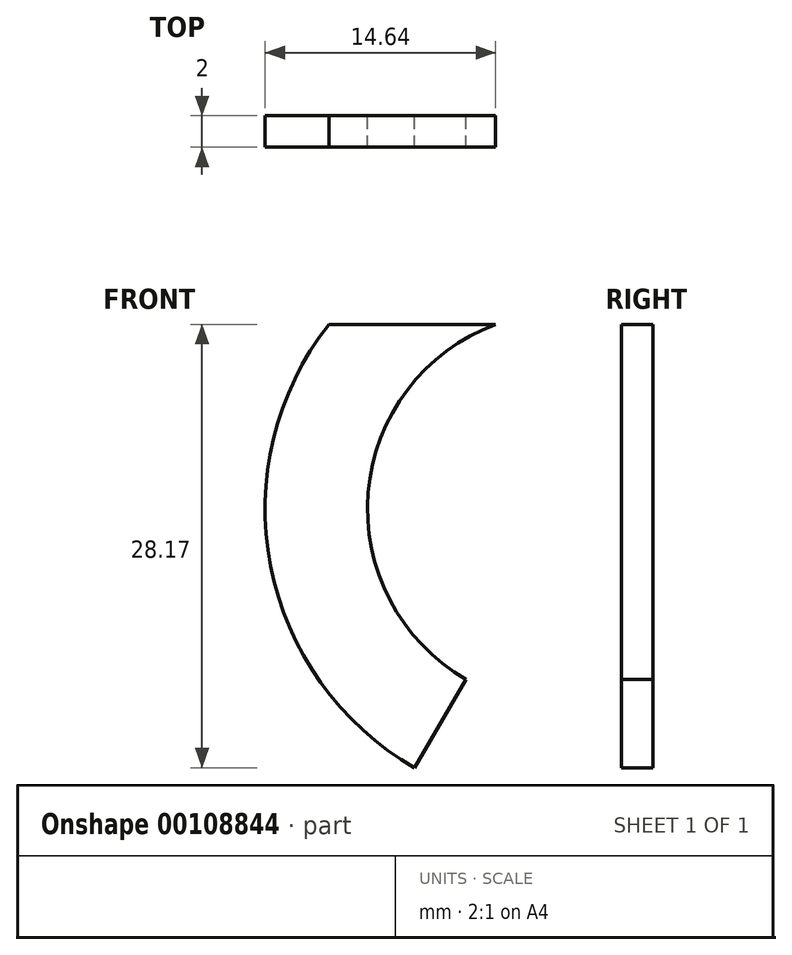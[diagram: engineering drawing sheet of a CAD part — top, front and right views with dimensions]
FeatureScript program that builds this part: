
annotation { "Feature Type Name" : "Feature", "Feature Type Description" : "" }
export const myFeature = defineFeature(function(context is Context, id is Id, definition is map)
    precondition{}
    {
        {
            var Q0;
            Q0=qCreatedBy(makeId("Front.planeOp"),FACE);
            var sketch = newSketch(context, id + "F0", { "sketchPlane" : qUnion([Q0])});
            skLineSegment(sketch, "E0", {"start": v(0, 23.45) * mm, "end": v(0, -32.3) * mm, "construction": true});
            skLineSegment(sketch, "E1", {"start": v(-31.08, 0) * mm, "end": v(27.8, 0) * mm, "construction": true});
            skLineSegment(sketch, "E2.MirrorCS", {"start": v(-6.25, -10.83) * mm, "end": v(-9.5, -16.45) * mm});
            skPoint(sketch, "E3.orphan", {"position": v(-15.77, -27.32) * mm});
            skPoint(sketch, "E4.orphan", {"position": v(15.77, -27.32) * mm});
            skPoint(sketch, "E5.orphan", {"position": v(0, 0) * mm});
            skLineSegment(sketch, "E6", {"start": v(-9.5, -16.45) * mm, "end": v(-50.88, -16.45) * mm, "construction": true});
            skLineSegment(sketch, "E7", {"start": v(-54.43, 11.72) * mm, "end": v(45.1, 11.72) * mm, "construction": true});
            skLineSegment(sketch, "E8", {"start": v(-14.96, 11.72) * mm, "end": v(-4.36, 11.72) * mm});
            skPoint(sketch, "E8.endSnap0", {"position": v(-4.66, 11.72) * mm});
            skArc(sketch, "E9.trimOffspring", {"start": v(-14.96, 11.72) * mm, "mid": v(-18.65, -3.61) * mm, "end": v(-9.5, -16.45) * mm});
            skArc(sketch, "E10.trimOffspring", {"start": v(-4.36, 11.72) * mm, "mid": v(-12.46, 1.05) * mm, "end": v(-6.25, -10.83) * mm});
            skSolve(sketch);
        }
        {
            var Q0;
            Q0 = qSketchRegion(id + "F0", true);
            extrude(context, id + "F1", {"entities" : qUnion([Q0]), "depth" : 2 * mm});
        }
    });
